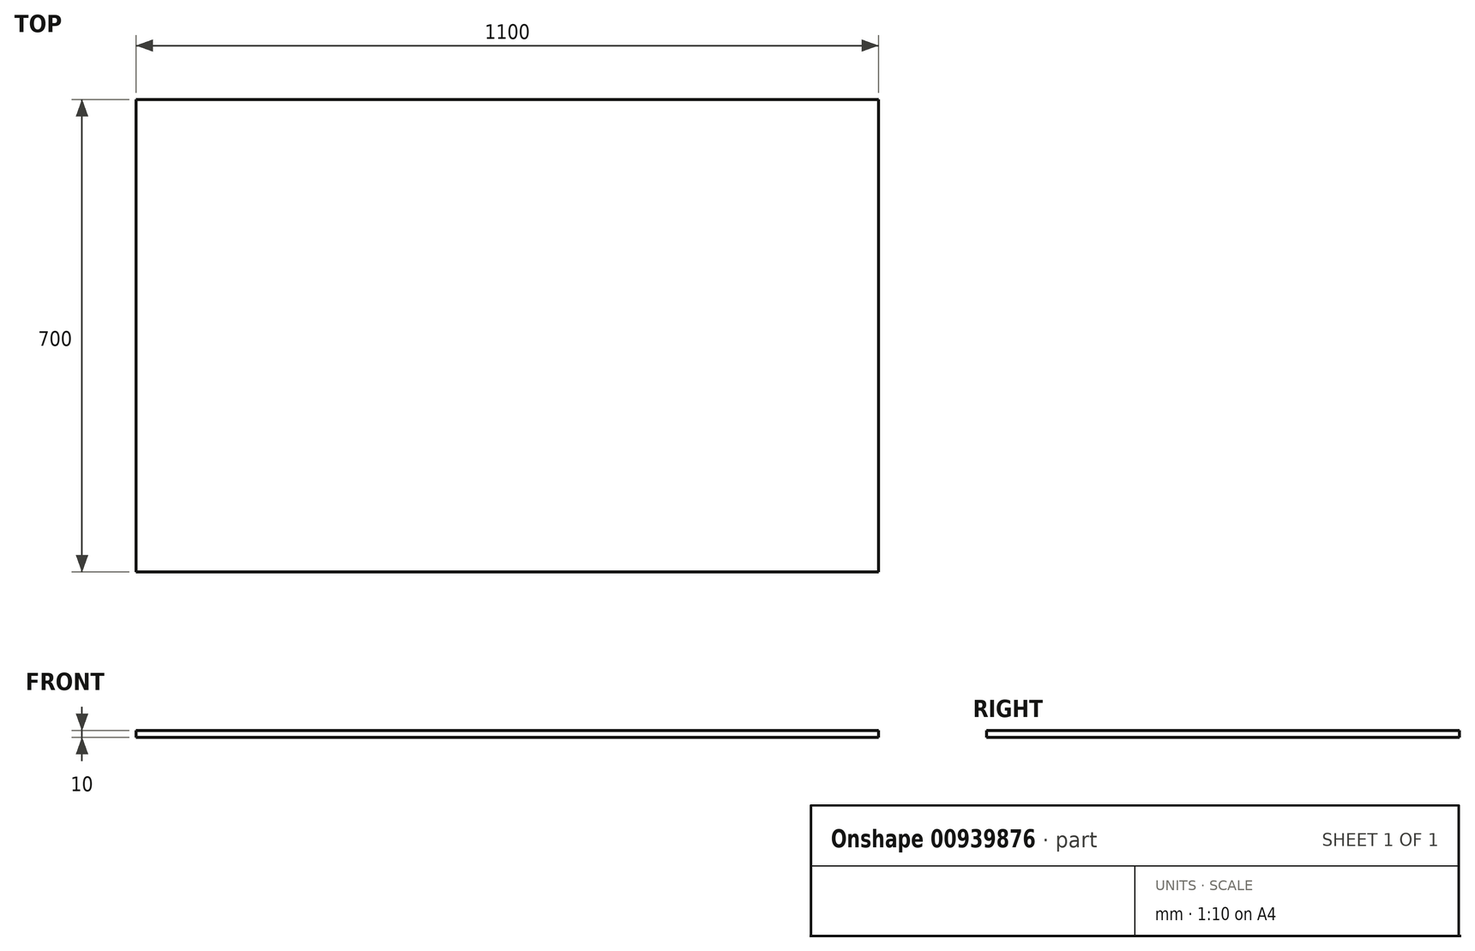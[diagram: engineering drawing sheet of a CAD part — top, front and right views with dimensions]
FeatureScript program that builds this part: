
annotation { "Feature Type Name" : "Feature", "Feature Type Description" : "" }
export const myFeature = defineFeature(function(context is Context, id is Id, definition is map)
    precondition{}
    {
        {
            var Q0;
            Q0=qCreatedBy(makeId("Top.planeOp"),FACE);
            var sketch = newSketch(context, id + "F0", { "sketchPlane" : qUnion([Q0])});
            skLineSegment(sketch, "E0.bottom", {"start": v(-550, 350) * mm, "end": v(550, 350) * mm});
            skLineSegment(sketch, "E0.top", {"start": v(-550, -350) * mm, "end": v(550, -350) * mm});
            skLineSegment(sketch, "E0.left", {"start": v(-550, 350) * mm, "end": v(-550, -350) * mm});
            skLineSegment(sketch, "E0.right", {"start": v(550, 350) * mm, "end": v(550, -350) * mm});
            skPoint(sketch, "E0.middle", {"position": v(0, 0) * mm});
            skSolve(sketch);
        }
        {
            var Q0;
            Q0=makeQuery(id+"F0.imprint","IMPRINT",FACE,{"disambiguationData":[TD([[makeQuery(id+"F0.imprint","IMPRINT",EDGE,{"derivedFrom":sQuery(id+"F0.wireOp",EDGE,"E0.bottom")}),-1.0]])]});
            extrude(context, id + "F1", {"entities" : qUnion([Q0]), "depth" : 10 * mm, "offsetDistance" : 25 * mm});
        }
    });
